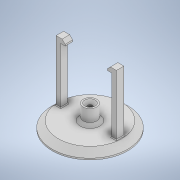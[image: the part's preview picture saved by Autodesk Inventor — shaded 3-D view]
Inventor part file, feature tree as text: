
AUTODESK INVENTOR PART (.ipt)
format: ipt  version: 2020.4 (Build 244396000, 396)  size: 168,448 bytes
history: native  units: in
note: dims shown in document units (in); Inventor stores cm internally (conversion verified against a paired STEP export)
features: chamfer x5, extrude x4, sketch x4, mirror x1
ambient origin geometry x8: Origin, YZ Plane, XZ Plane, XY Plane, X Axis, Y Axis, Z Axis, Center Point
bodies: Solid1 (feature_tree)
feature tree (14):
  extrude  "Extrusion1"  Depth=0.1969in TaperAngle=0.0deg
  chamfer  "Chamfer1"  Distance=0.1575in Angle=45.0deg
  extrude  "Extrusion2"  Depth=0.3937in
  chamfer  "Chamfer2"  Distance=0.3937in
  chamfer  "Chamfer3"  Distance=0.0787in Angle=45.0deg
  extrude  "Extrusion3"  Depth=0.1181in
  extrude  "Extrusion4"  Depth=1.5748in TaperAngle=0.0deg
  chamfer  "Chamfer4"  Distance=0.1181in
  mirror  "Mirror1"
  chamfer  "Chamfer6"  Distance=0.1181in
  sketch  "Sketch1"  dims[d0=1.9685in d1=0.1969in d2=0.0in d3=0.1575in d4=0.0787in d5=45.0deg]
  sketch  "Sketch2"  dims[d6=0.1181in d7=0.3543in d8=0.3937in d9=0.0in d10=0.0787in d11=0.0787in d12=45.0deg]
  sketch  "Sketch3"  dims[d13=0.0787in d14=0.0787in d15=45.0deg d16=0.1181in]
  sketch  "Sketch4"  dims[d17=0.1969in d18=1.5748in d19=0.0in d20=0.1181in d21=0.1181in d22=0.0in d23=0.0787in d24=0.0787in d25=45.0deg d29=0.6693in d30=0.0197in d31=0.0787in d32=45.0deg]
